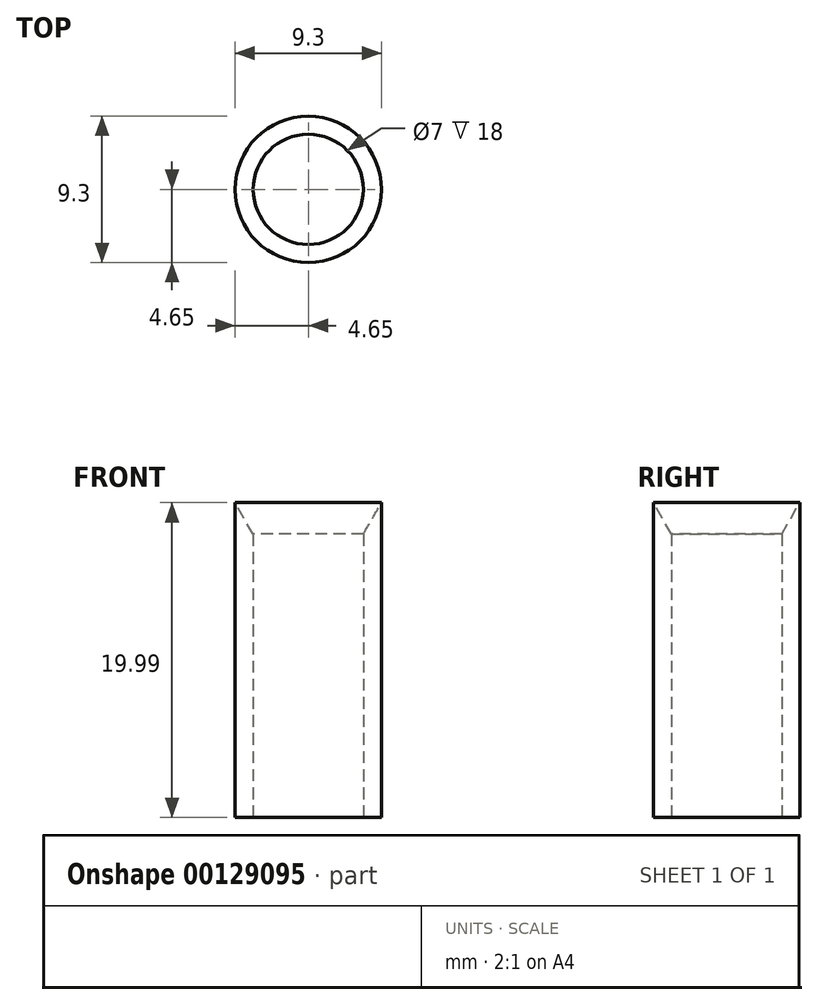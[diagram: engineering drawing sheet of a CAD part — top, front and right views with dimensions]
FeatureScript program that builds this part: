
annotation { "Feature Type Name" : "Feature", "Feature Type Description" : "" }
export const myFeature = defineFeature(function(context is Context, id is Id, definition is map)
    precondition{}
    {
        {
            var Q0;
            Q0=qCreatedBy(makeId("Top.planeOp"),FACE);
            var sketch = newSketch(context, id + "F0", { "sketchPlane" : qUnion([Q0])});
            skCircle(sketch, "E0", {"center": v(0, 0) * mm, "radius": 4.65 * mm});
            skCircle(sketch, "E1", {"center": v(0, 0) * mm, "radius": 3.5 * mm});
            skSolve(sketch);
        }
        {
            var Q0;
            Q0 = qSketchRegion(id + "F0", true);
            extrude(context, id + "F1", {"entities" : qUnion([Q0]), "depth" : 20 * mm});
        }
        {
            var Q0;
            Q0=makeQuery(id+"F1.opExtrude","CAP_EDGE",EDGE,{"disambiguationData":[OSD([sQuery(id+"F0.wireOp",EDGE,"E1")])],"isStart":false});
            chamfer(context, id + "F2", {"entities" : qUnion([Q0]), "chamferType" : ChamferType.OFFSET_ANGLE, "width" : 2 * mm, "oppositeDirection" : false, "angle" : 30 * degree, "tangentPropagation" : true});
        }
    });
